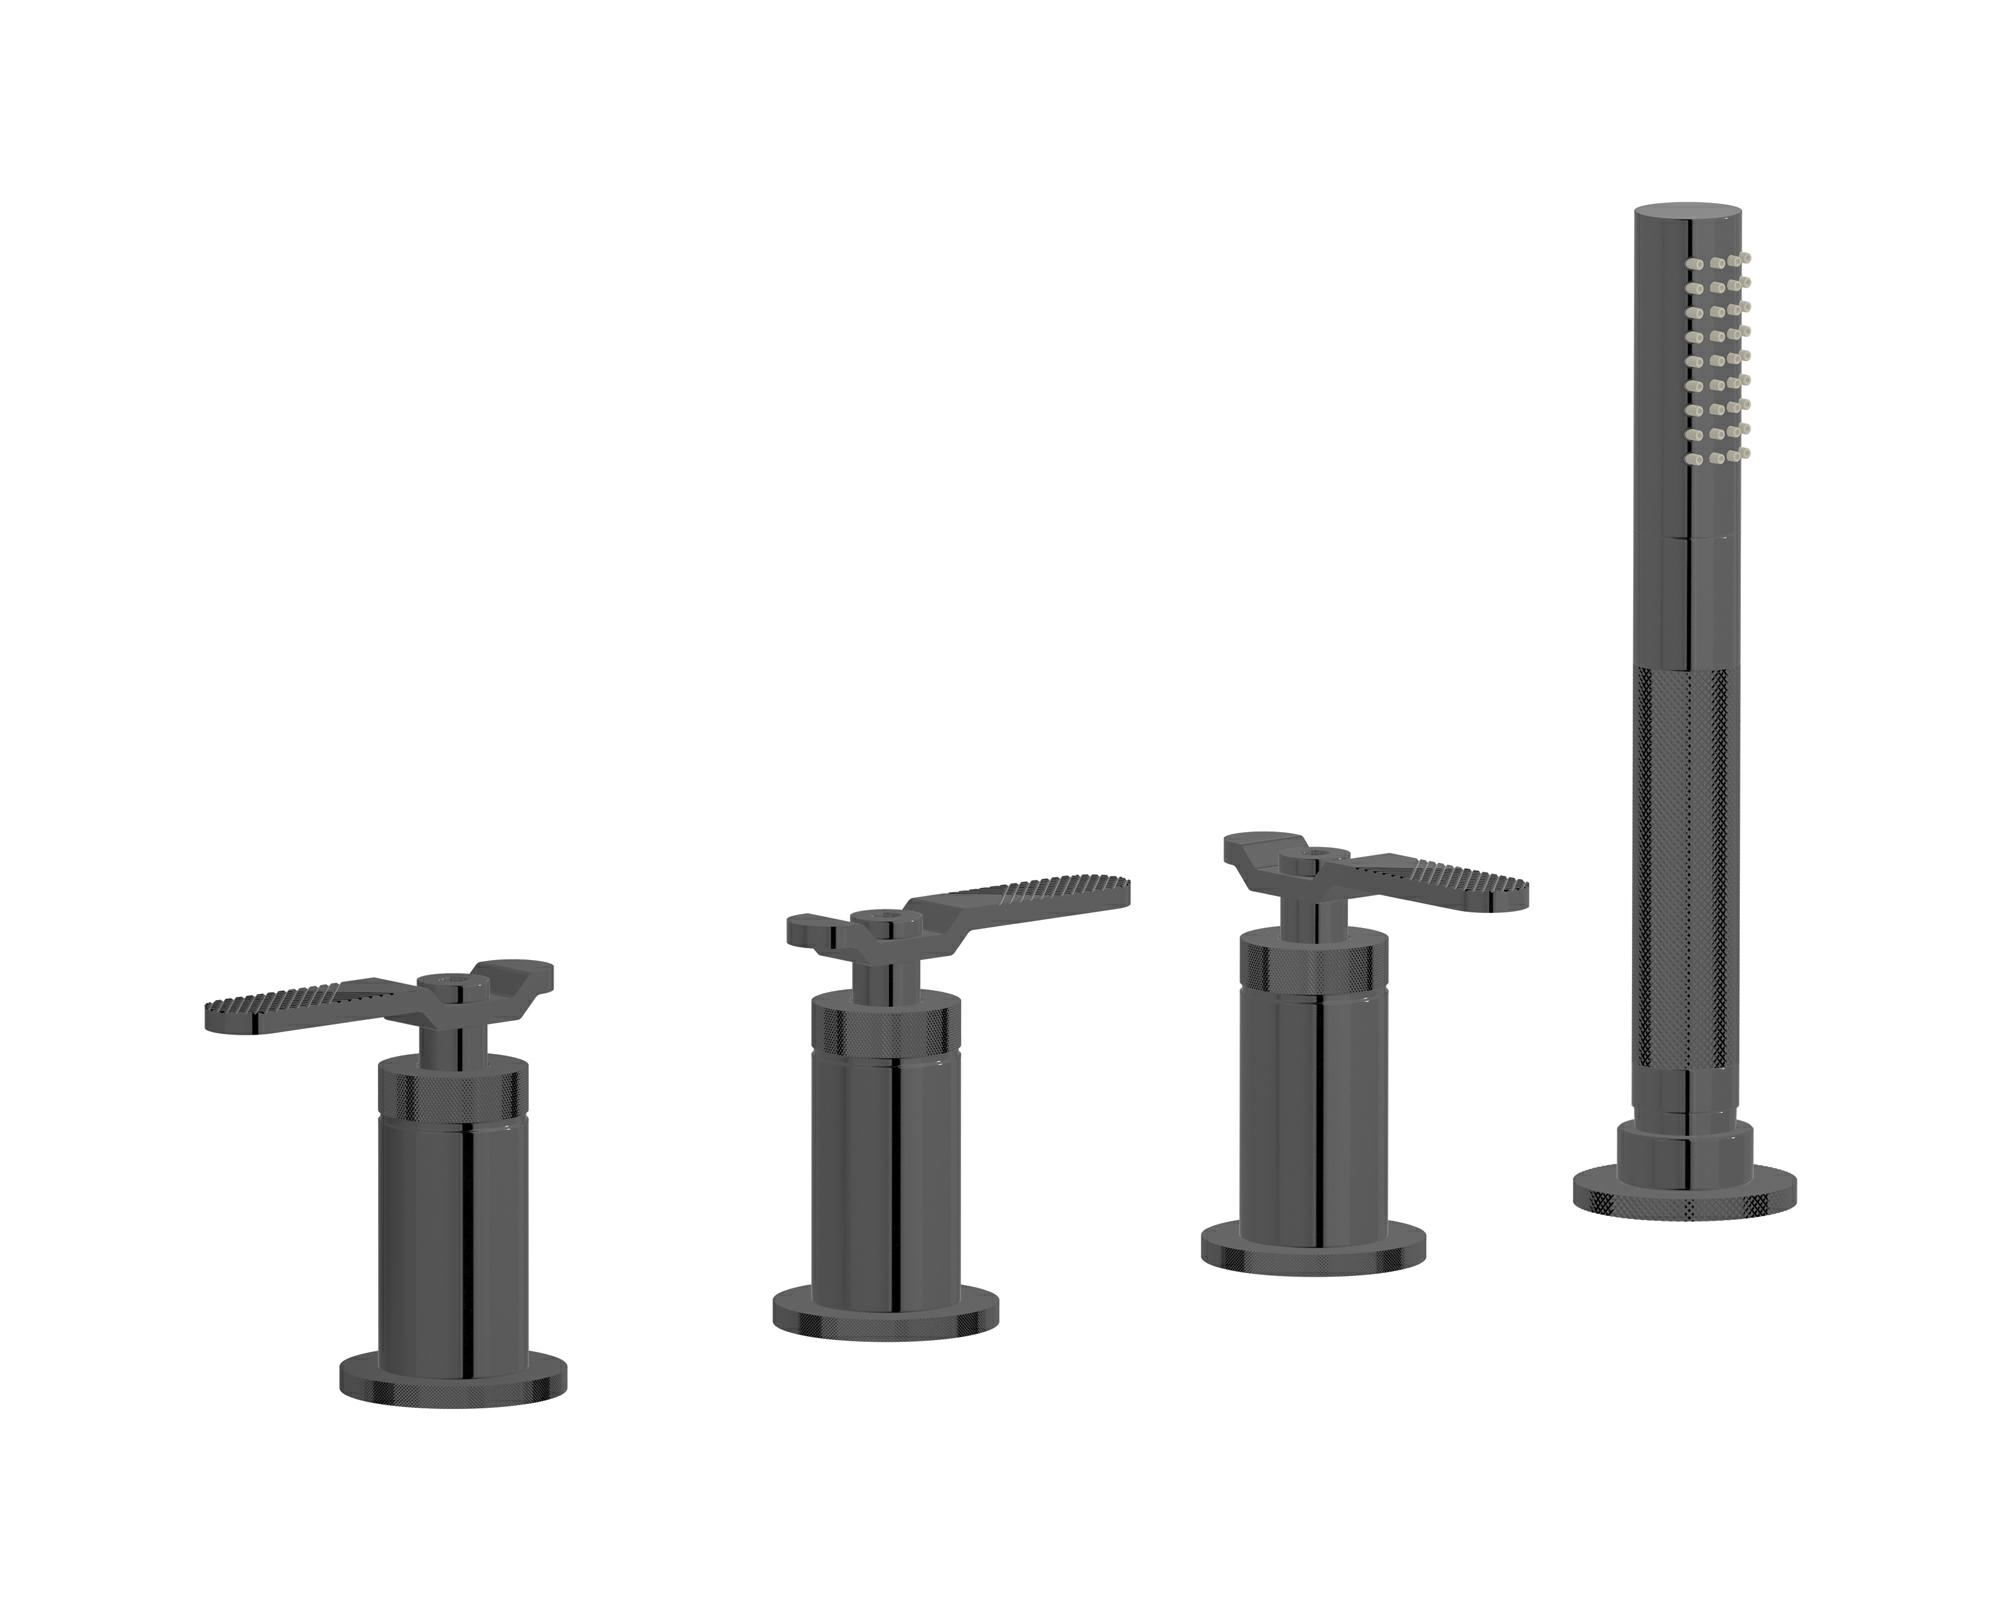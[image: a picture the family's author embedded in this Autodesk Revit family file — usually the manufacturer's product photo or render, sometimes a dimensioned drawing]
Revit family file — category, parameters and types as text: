
# Revit family: B2397
name_source: partatom
category: Apparecchi idraulici
units: mm (PartAtom-declared; Revit-internal decimal feet)

## family parameters
Basato su piano di lavoro = No
Condiviso = No
Mantieni orientamento annotazione = No
Numero OmniClass = 23.45.55.17
Punto di calcolo locali = No
Quota connettore circolare = Usa diametro
Sempre verticale = Sì
Taglio con vuoti quando caricato = No
Tipo di parte = Normale
Titolo OmniClass = Mixing Faucets

## types (13) — shared parameters
Cold water inlet = 10 mm  [stored 0.0328084 ft]
Commenti sul tipo = Four holes bath filler with overflow outlet connection, diverter and shower kit
Connessione CW = No
Connessione HW = No
Connessione di scarico = No
Connessione di ventilazione = No
Descrizione = Four holes bath filler with overflow outlet connection, diverter and shower kit
Hot water inlet = 10 mm  [stored 0.0328084 ft]
Produttore = IB Rubinetterie S.p.A.
URL = https://www.weareib.it
zero-valued in all types: Prospetto di default

## per-type parameters (varying)
| type | Finishes surface | Immagine tipo | Modello |
| Chrome | IB_Chrome | B2397CC.jpg | B2397CC |
| Black Chrome | IB_Black chrome | B2397CF.jpg | B2397CF |
| Brushed Black Chrome | IB_Brushed black chrome | B2397CS.jpg | B2397CS |
| Pale Gold | IB_Pale gold | B2397II.jpg | B2397II |
| Brushed Pale Gold | IB_brushed pale gold | B2397IS.jpg | B2397IS |
| Matt Black | IB_matt black | B2397NP.jpg | B2397NP |
| Natural Brass | IB_Brass | B2397ON.jpg | B2397ON |
| Gold | IB_gold | B2397OO.jpg | B2397OO |
| Brushed Gold | IB_brushed gold | B2397OS.jpg | B2397OS |
| Rose Gold | IB_Rose gold | B2397RS.jpg | B2397RS |
| Brushed Rose Gold | IB_Brushed rose gold | B2397SR.jpg | B2397SR |
| Brushed Nickel | IB_Brushed nickel | B2397SS.jpg | B2397SS |
| Modern Bronze | IB_Modern bronze | B2397MB.jpg | B2397MB |

note: [stored X ft] marks values corroborated as IEEE doubles in the binary element streams (Revit-internal decimal feet)
